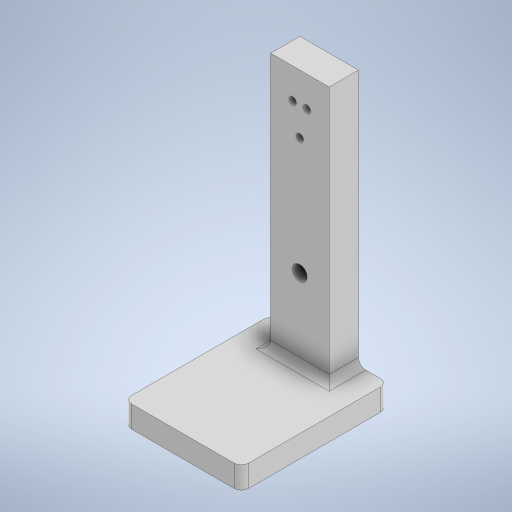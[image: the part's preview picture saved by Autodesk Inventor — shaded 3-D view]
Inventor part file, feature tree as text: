
AUTODESK INVENTOR PART (.ipt)
format: ipt  version: 2023 (Build 270158000, 158)  size: 273,408 bytes
history: native  units: in
note: dims shown in document units (in); Inventor stores cm internally (conversion verified against a paired STEP export)
features: extrude x3, sketch x2, fillet x2
ambient origin geometry x8: Origin, YZ Plane, XZ Plane, XY Plane, X Axis, Y Axis, Z Axis, Center Point
bodies: Solid1 (feature_tree)
feature tree (7):
  sketch  "Sketch1"  dims[d0=4.375in d1=0.5in]
  extrude  "Extrusion1"  Depth=0.5in
  extrude  "Extrusion2"  Depth=2.5in
  extrude  "Extrusion3"  Depth=1.0in TaperAngle=0.0deg
  fillet  "Fillet1"  Radius=0.25in
  fillet  "Fillet2"  Radius=0.125in
  sketch  "Sketch2"  dims[d2=4.75in d3=2.5in d4=1.0in d5=0.0in d7=0.25in d8=0.125in d9=1.375in d10=2.0in d11=0.125in d12=0.5in d17=0.125in d18=0.5in d20=1.0in d21=0.0in d22=0.1213in d23=0.1213in d24=1.5in d25=0.5in d26=0.0in d27=0.0in d28=0.125in d29=0.125in]
